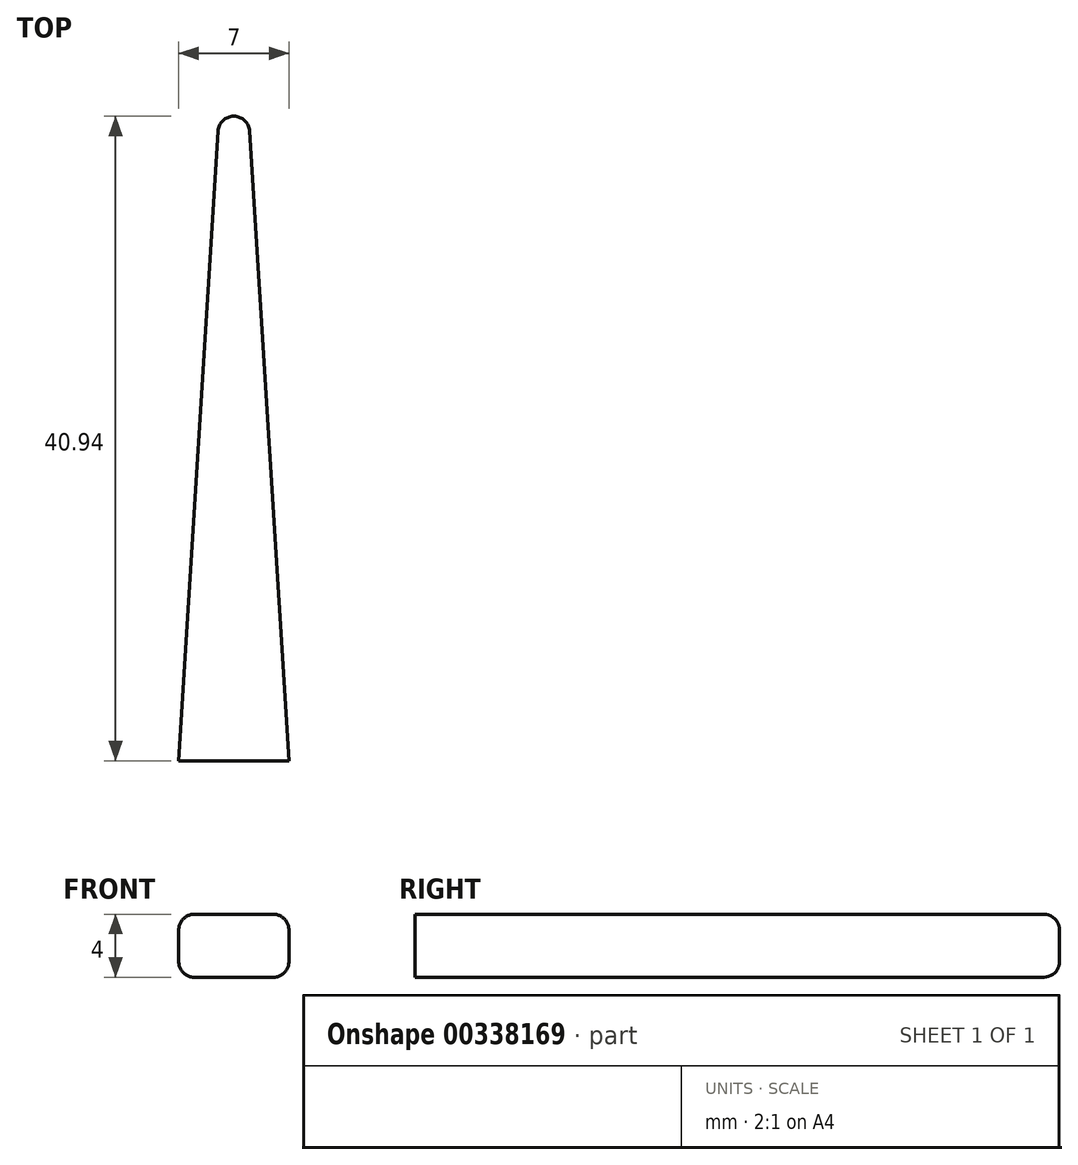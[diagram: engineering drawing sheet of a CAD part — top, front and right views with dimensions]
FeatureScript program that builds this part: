
annotation { "Feature Type Name" : "Feature", "Feature Type Description" : "" }
export const myFeature = defineFeature(function(context is Context, id is Id, definition is map)
    precondition{}
    {
        {
            var Q0;
            Q0=qCreatedBy(makeId("Top.planeOp"),FACE);
            var sketch = newSketch(context, id + "F0", { "sketchPlane" : qUnion([Q0])});
            skLineSegment(sketch, "E0", {"start": v(0, 40) * mm, "end": v(0, 0) * mm, "construction": true});
            skLineSegment(sketch, "E1", {"start": v(-3.5, 0) * mm, "end": v(3.5, 0) * mm, "construction": true});
            skLineSegment(sketch, "E2", {"start": v(-1, 40) * mm, "end": v(1, 40) * mm, "construction": true});
            skLineSegment(sketch, "E3", {"start": v(-3.5, 0) * mm, "end": v(-1, 40) * mm});
            skLineSegment(sketch, "E4", {"start": v(3.5, 0) * mm, "end": v(1, 40) * mm});
            skArc(sketch, "E5", {"start": v(1, 40) * mm, "mid": v(0, 40.94) * mm, "end": v(-1, 40) * mm});
            skLineSegment(sketch, "E6", {"start": v(-3.5, 0) * mm, "end": v(3.5, 0) * mm});
            skSolve(sketch);
        }
        {
            var Q0;
            Q0=makeQuery(id+"F0.imprint","IMPRINT",FACE,{"disambiguationData":[TD([[makeQuery(id+"F0.imprint","IMPRINT",EDGE,{"derivedFrom":sQuery(id+"F0.wireOp",EDGE,"E3")}),-1.0]])]});
            extrude(context, id + "F1", {"entities" : qUnion([Q0]), "depth" : 4 * mm});
        }
        {
            var Q0;
            Q0=makeQuery(id+"F1.opExtrude","CAP_EDGE",EDGE,{"disambiguationData":[OSD([sQuery(id+"F0.wireOp",EDGE,"E3")])],"isStart":false});
            var Q1;
            Q1=makeQuery(id+"F1.opExtrude","CAP_EDGE",EDGE,{"disambiguationData":[OSD([sQuery(id+"F0.wireOp",EDGE,"E3")])],"isStart":true});
            var Q2;
            Q2=makeQuery(id+"F1.opExtrude","CAP_EDGE",EDGE,{"disambiguationData":[OSD([sQuery(id+"F0.wireOp",EDGE,"E4")])],"isStart":false});
            var Q3;
            Q3=makeQuery(id+"F1.opExtrude","CAP_EDGE",EDGE,{"disambiguationData":[OSD([sQuery(id+"F0.wireOp",EDGE,"E4")])],"isStart":true});
            fillet(context, id + "F2", {"entities" : qUnion([Q0, Q1, Q2, Q3]), "radius" : 1 * mm, "tangentPropagation" : true, "allowEdgeOverflow" : false});
        }
    });
